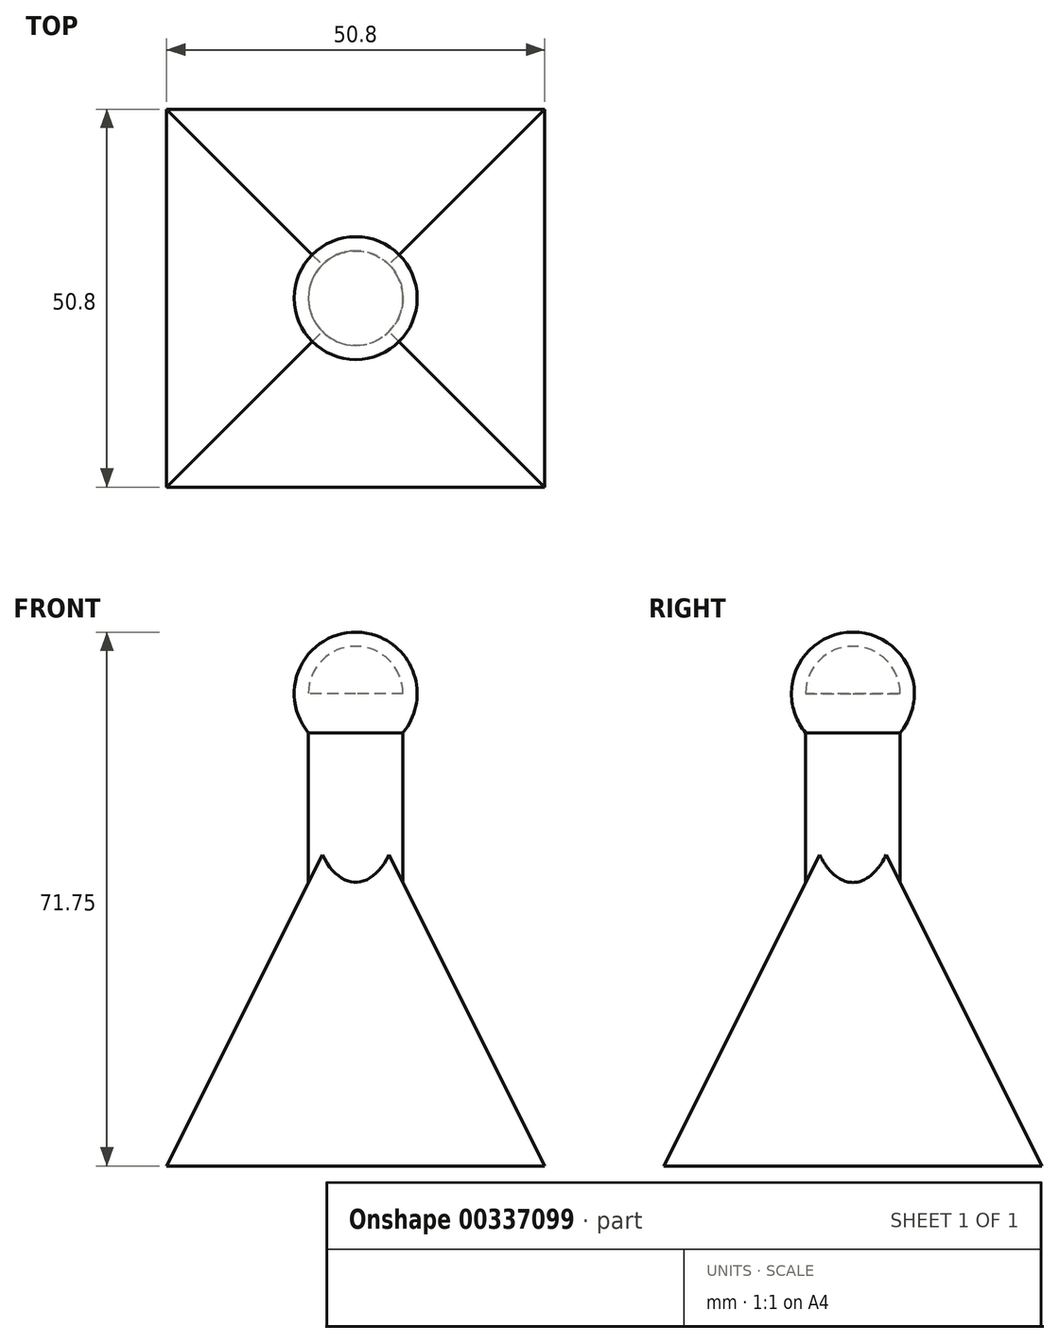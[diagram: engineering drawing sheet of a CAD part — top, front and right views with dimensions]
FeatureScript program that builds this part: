
annotation { "Feature Type Name" : "Feature", "Feature Type Description" : "" }
export const myFeature = defineFeature(function(context is Context, id is Id, definition is map)
    precondition{}
    {
        {
            var Q0;
            Q0=qCreatedBy(makeId("Top.planeOp"),FACE);
            var sketch = newSketch(context, id + "F0", { "sketchPlane" : qUnion([Q0])});
            skLineSegment(sketch, "E0.bottom", {"start": v(-25.4, 25.4) * mm, "end": v(25.4, 25.4) * mm});
            skLineSegment(sketch, "E0.top", {"start": v(-25.4, -25.4) * mm, "end": v(25.4, -25.4) * mm});
            skLineSegment(sketch, "E0.left", {"start": v(-25.4, 25.4) * mm, "end": v(-25.4, -25.4) * mm});
            skLineSegment(sketch, "E0.right", {"start": v(25.4, 25.4) * mm, "end": v(25.4, -25.4) * mm});
            skPoint(sketch, "E0.middle", {"position": v(0, 0) * mm});
            skSolve(sketch);
        }
        {
            var Q0;
            Q0=qCreatedBy(makeId("Top.planeOp"),FACE);
            cPlane(context, id + "F1", {"entities" : qUnion([Q0]), "cplaneType" : CPlaneType.OFFSET, "offset" : 50.8 * mm, "width" : 152.4 * mm, "height" : 152.4 * mm});
        }
        {
            var Q0;
            Q0=qCreatedBy(id+"F1.planeOp",FACE);
            var sketch = newSketch(context, id + "F2", { "sketchPlane" : qUnion([Q0])});
            skPoint(sketch, "E1", {"position": v(0, 0) * mm});
            skSolve(sketch);
        }
        {
            var Q0;
            Q0 = qSketchRegion(id + "F0", true);
            var Q1;
            Q1=sQuery(id+"F2.wireOp",VERTEX,"E1");
            loft(context, id + "F3", {"sheetProfilesArray" : [{ "sheetProfileEntities" : qUnion([Q0]) }, { "sheetProfileEntities" : qUnion([Q1]) }]});
        }
        {
            var Q0;
            Q0=qCreatedBy(id+"F1.planeOp",FACE);
            var sketch = newSketch(context, id + "F4", { "sketchPlane" : qUnion([Q0])});
            skCircle(sketch, "E2", {"center": v(0, 0) * mm, "radius": 6.35 * mm});
            skSolve(sketch);
        }
        {
            var Q0;
            Q0 = qSketchRegion(id + "F4", true);
            var Q1;
            Q1=sQuery(id+"F4.wireOp",EDGE,"E2");
            extrude(context, id + "F5", {"entities" : qUnion([Q0]), "operationType" : NewBodyOperationType.ADD, "surfaceEntities" : qUnion([Q1]), "oppositeDirection" : true, "depth" : 25.4 * mm, "hasSecondDirection" : true, "secondDirectionOppositeDirection" : false, "secondDirectionDepth" : 12.7 * mm});
        }
        {
            var Q0;
            Q0=makeQuery(id+"F5.opExtrude","CAP_FACE",FACE,{"disambiguationData":[OSD([sQuery(id+"F4.wireOp",EDGE,"E2")])],"isStart":true});
            var sketch = newSketch(context, id + "F6", { "sketchPlane" : qUnion([Q0])});
            skArc(sketch, "E3", {"start": v(0, -8.26) * mm, "mid": v(8.26, 0) * mm, "end": v(0, 8.26) * mm});
            skLineSegment(sketch, "E4", {"start": v(0, 8.26) * mm, "end": v(0, -8.26) * mm});
            skPoint(sketch, "E5.orphan", {"position": v(0, 26.08) * mm});
            skSolve(sketch);
        }
        {
            var Q0;
            {var subQ0=sQuery(id+"F6.wireOp",EDGE,"E3");Q0=makeQuery(id+"F6.imprint","IMPRINT",FACE,{"disambiguationData":[TD([[makeQuery(id+"F6.imprint","IMPRINT",EDGE,{"derivedFrom":subQ0}),1.0]])]});}
            var Q1;
            Q1=sQuery(id+"F6.wireOp",EDGE,"E4");
            revolve(context, id + "F7", {"operationType" : NewBodyOperationType.ADD, "entities" : qUnion([Q0]), "axis" : qUnion([Q1]), "revolveType" : RevolveType.FULL});
        }
    });
